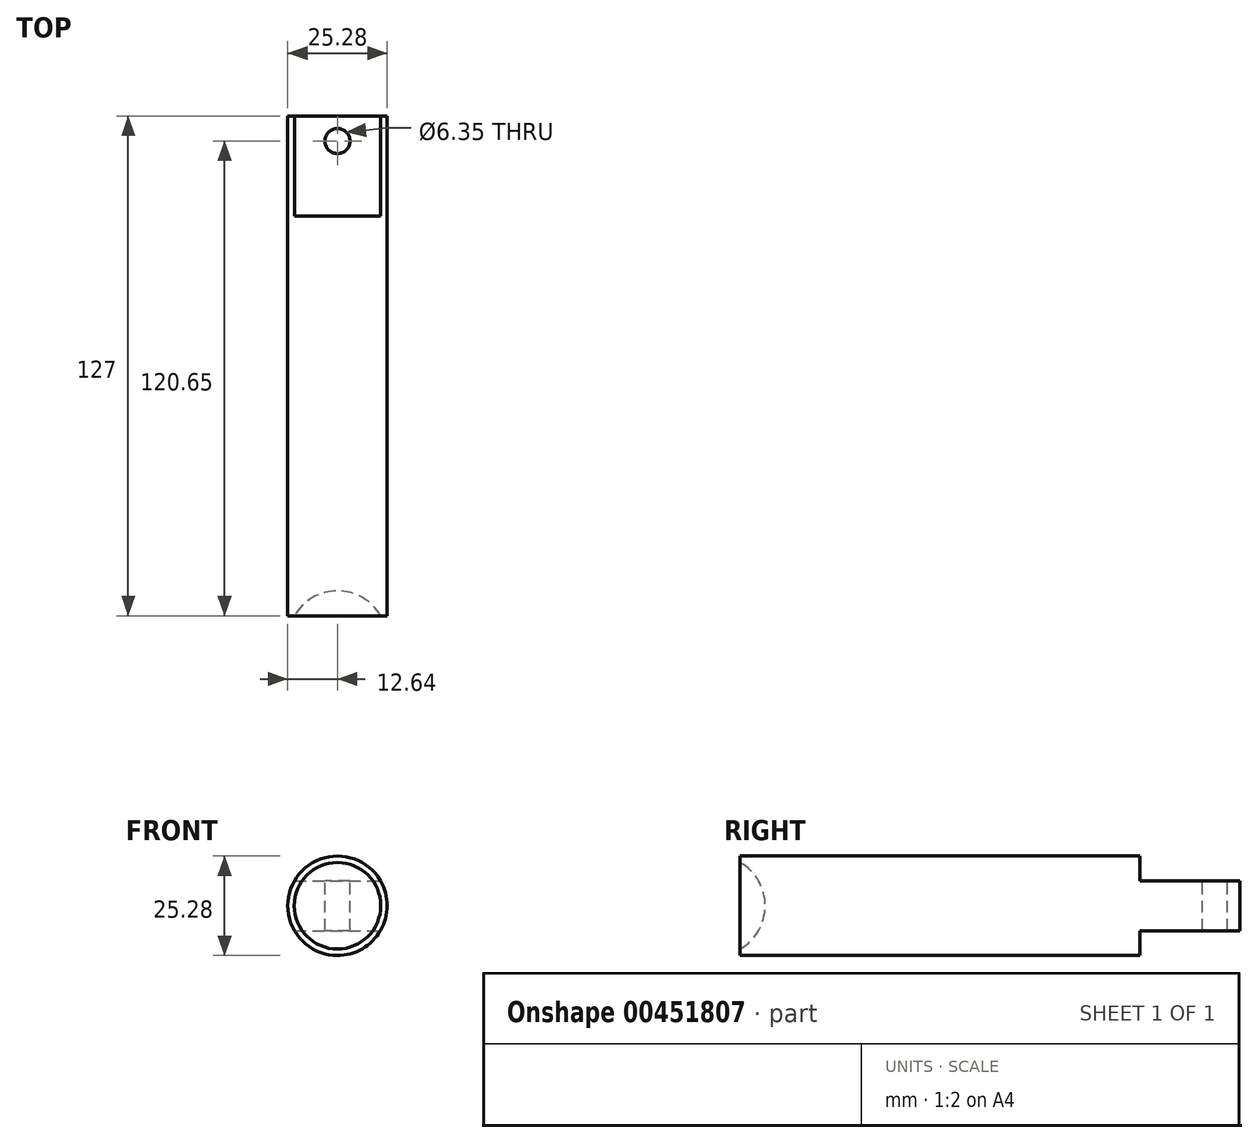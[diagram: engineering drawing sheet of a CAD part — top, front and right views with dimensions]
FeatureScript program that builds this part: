
annotation { "Feature Type Name" : "Feature", "Feature Type Description" : "" }
export const myFeature = defineFeature(function(context is Context, id is Id, definition is map)
    precondition{}
    {
        {
            var Q0;
            Q0=qCreatedBy(makeId("Front.planeOp"),FACE);
            var sketch = newSketch(context, id + "F0", { "sketchPlane" : qUnion([Q0])});
            skCircle(sketch, "E0", {"center": v(0, 0) * mm, "radius": 12.64 * mm});
            skSolve(sketch);
        }
        {
            var Q0;
            Q0 = qSketchRegion(id + "F0", true);
            extrude(context, id + "F1", {"entities" : qUnion([Q0]), "endBound" : BoundingType.SYMMETRIC, "depth" : 127 * mm});
        }
        {
            var Q0;
            Q0=qCreatedBy(makeId("Right.planeOp"),FACE);
            var sketch = newSketch(context, id + "F2", { "sketchPlane" : qUnion([Q0])});
            skLineSegment(sketch, "E1.bottom", {"start": v(63.5, 6.35) * mm, "end": v(38.1, 6.35) * mm});
            skLineSegment(sketch, "E1.top", {"start": v(63.5, 24.65) * mm, "end": v(38.1, 24.65) * mm});
            skLineSegment(sketch, "E1.left", {"start": v(63.5, 6.35) * mm, "end": v(63.5, 24.65) * mm});
            skLineSegment(sketch, "E1.right", {"start": v(38.1, 6.35) * mm, "end": v(38.1, 24.65) * mm});
            skLineSegment(sketch, "E2", {"start": v(0, 0) * mm, "end": v(17.27, 0) * mm, "construction": true});
            skLineSegment(sketch, "E3.MirrorCS", {"start": v(63.5, -6.35) * mm, "end": v(38.1, -6.35) * mm});
            skLineSegment(sketch, "E4.MirrorCS", {"start": v(63.5, -24.65) * mm, "end": v(38.1, -24.65) * mm});
            skLineSegment(sketch, "E5.MirrorCS", {"start": v(63.5, -6.35) * mm, "end": v(63.5, -24.65) * mm});
            skLineSegment(sketch, "E6.MirrorCS", {"start": v(38.1, -6.35) * mm, "end": v(38.1, -24.65) * mm});
            skSolve(sketch);
        }
        {
            var Q0;
            Q0 = qSketchRegion(id + "F2", true);
            extrude(context, id + "F3", {"entities" : qUnion([Q0]), "operationType" : NewBodyOperationType.REMOVE, "endBound" : BoundingType.SYMMETRIC, "oppositeDirection" : true, "depth" : 25.4 * mm});
        }
        {
            var Q0;
            Q0=makeQuery(id+"F3.boolean.opBoolean","COPY",FACE,{"derivedFrom":makeQuery(id+"F3.opExtrude","SWEPT_FACE",FACE,{"disambiguationData":[OSD([sQuery(id+"F2.wireOp",EDGE,"E1.bottom")])]})});
            var sketch = newSketch(context, id + "F4", { "sketchPlane" : qUnion([Q0])});
            skCircle(sketch, "E7", {"center": v(0, 57.15) * mm, "radius": 3.18 * mm});
            skSolve(sketch);
        }
        {
            var Q0;
            Q0 = qSketchRegion(id + "F4", true);
            extrude(context, id + "F5", {"entities" : qUnion([Q0]), "operationType" : NewBodyOperationType.REMOVE, "oppositeDirection" : true, "depth" : 25.4 * mm});
        }
        {
            var Q0;
            Q0=qCreatedBy(makeId("Right.planeOp"),FACE);
            var sketch = newSketch(context, id + "F6", { "sketchPlane" : qUnion([Q0])});
            skArc(sketch, "E8", {"start": v(-69.85, -12.7) * mm, "mid": v(-57.15, 0) * mm, "end": v(-69.85, 12.7) * mm});
            skLineSegment(sketch, "E9", {"start": v(-69.85, 0) * mm, "end": v(-69.85, -12.7) * mm});
            skLineSegment(sketch, "E10", {"start": v(-69.85, -12.7) * mm, "end": v(-69.85, 12.7) * mm});
            skSolve(sketch);
        }
        {
            var Q0;
            Q0 = qSketchRegion(id + "F6", true);
            var Q1;
            Q1=sQuery(id+"F6.wireOp",EDGE,"E10");
            revolve(context, id + "F7", {"operationType" : NewBodyOperationType.REMOVE, "entities" : qUnion([Q0]), "axis" : qUnion([Q1]), "revolveType" : RevolveType.FULL, "oppositeDirection" : true});
        }
    });
